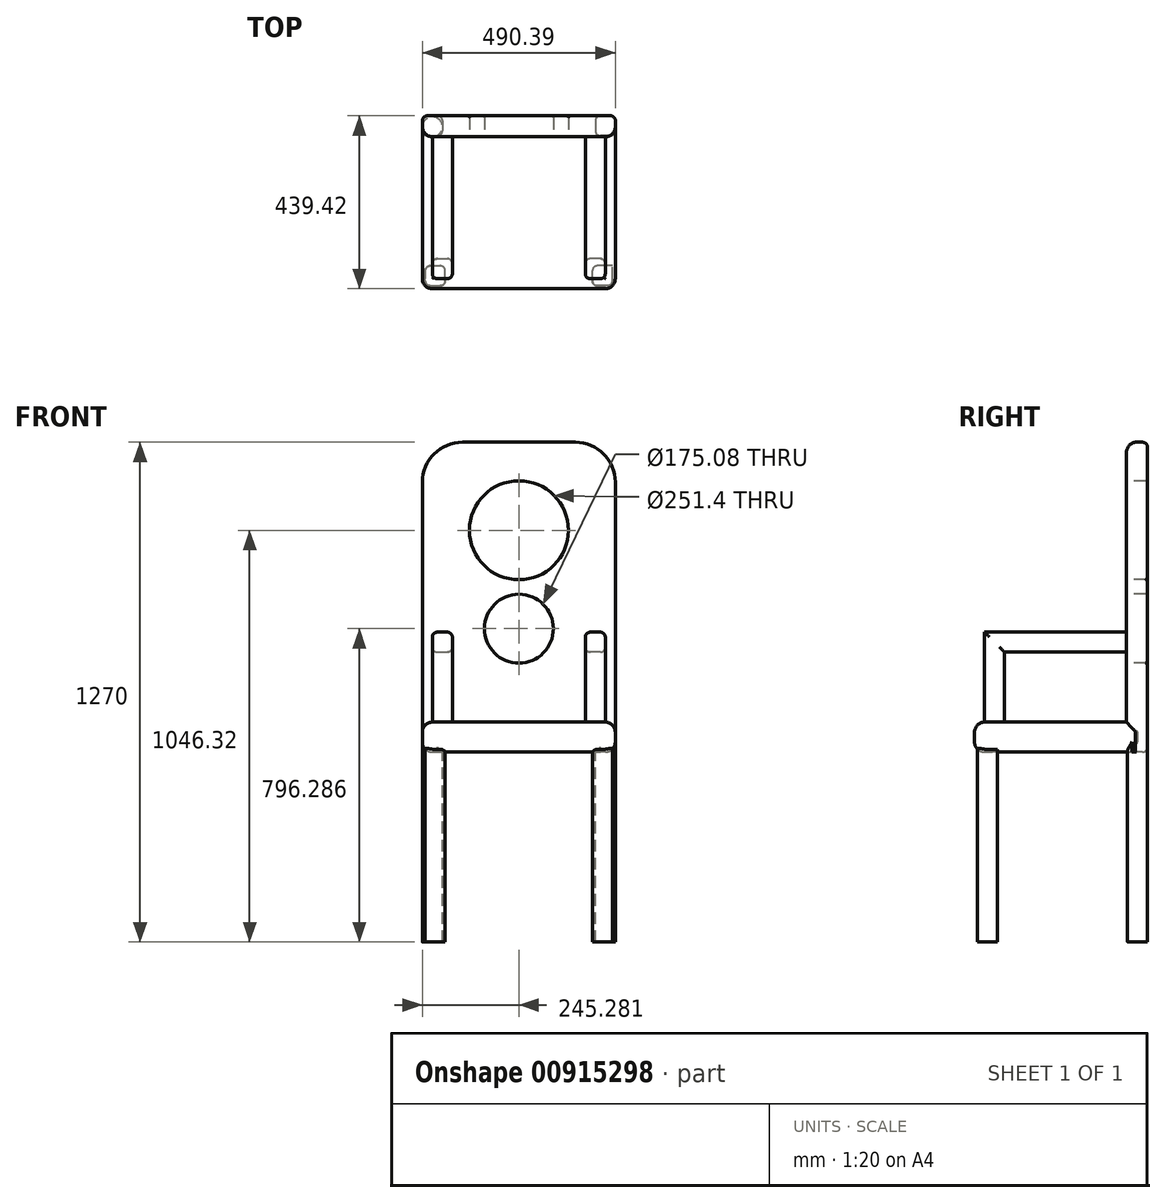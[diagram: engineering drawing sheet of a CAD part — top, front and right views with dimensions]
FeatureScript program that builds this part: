
annotation { "Feature Type Name" : "Feature", "Feature Type Description" : "" }
export const myFeature = defineFeature(function(context is Context, id is Id, definition is map)
    precondition{}
    {
        {
            var Q0;
            Q0=qCreatedBy(makeId("Top.planeOp"),FACE);
            var sketch = newSketch(context, id + "F0", { "sketchPlane" : qUnion([Q0])});
            skLineSegment(sketch, "E0.bottom", {"start": v(-206.15, 232.77) * mm, "end": v(284.07, 232.77) * mm});
            skLineSegment(sketch, "E0.top", {"start": v(-206.15, -181.25) * mm, "end": v(284.07, -181.25) * mm});
            skLineSegment(sketch, "E0.left", {"start": v(-206.15, 232.77) * mm, "end": v(-206.15, -181.25) * mm});
            skLineSegment(sketch, "E0.right", {"start": v(284.07, 232.77) * mm, "end": v(284.07, -181.25) * mm});
            skSolve(sketch);
        }
        {
            var Q0;
            Q0 = qSketchRegion(id + "F0", true);
            extrude(context, id + "F1", {"entities" : qUnion([Q0]), "depth" : 76.2 * mm, "offsetDistance" : 25.4 * mm});
        }
        {
            var Q0;
            Q0=makeQuery(id+"F1.opExtrude","CAP_EDGE",EDGE,{"disambiguationData":[OSD([sQuery(id+"F0.wireOp",EDGE,"E0.top")])],"isStart":false});
            var Q1;
            Q1=makeQuery(id+"F1.opExtrude","CAP_EDGE",EDGE,{"disambiguationData":[OSD([sQuery(id+"F0.wireOp",EDGE,"E0.left")])],"isStart":false});
            var Q2;
            Q2=makeQuery(id+"F1.opExtrude","SWEPT_EDGE",EDGE,{"disambiguationData":[OSD([sQuery(id+"F0.wireOp",EDGE,"E0.top"),sQuery(id+"F0.wireOp",EDGE,"E0.left")])]});
            var Q3;
            Q3=makeQuery(id+"F1.opExtrude","SWEPT_EDGE",EDGE,{"disambiguationData":[OSD([sQuery(id+"F0.wireOp",EDGE,"E0.top"),sQuery(id+"F0.wireOp",EDGE,"E0.right")])]});
            var Q4;
            Q4=makeQuery(id+"F1.opExtrude","CAP_EDGE",EDGE,{"disambiguationData":[OSD([sQuery(id+"F0.wireOp",EDGE,"E0.right")])],"isStart":false});
            fillet(context, id + "F2", {"entities" : qUnion([Q0, Q1, Q2, Q3, Q4]), "radius" : 25.4 * mm, "tangentPropagation" : true, "allowEdgeOverflow" : false});
        }
        {
            var Q0;
            Q0=makeQuery(id+"F1.opExtrude","SWEPT_FACE",FACE,{"disambiguationData":[OSD([sQuery(id+"F0.wireOp",EDGE,"E0.bottom")])]});
            cPlane(context, id + "F3", {"entities" : qUnion([Q0]), "cplaneType" : CPlaneType.OFFSET, "offset" : 25.4 * mm, "width" : 152.4 * mm, "height" : 152.4 * mm});
        }
        {
            var Q0;
            Q0=qCreatedBy(id+"F3.planeOp",FACE);
            var sketch = newSketch(context, id + "F4", { "sketchPlane" : qUnion([Q0])});
            skLineSegment(sketch, "E1.bottom", {"start": v(-284.24, 0) * mm, "end": v(205.98, 0) * mm});
            skLineSegment(sketch, "E1.top", {"start": v(-284.24, 787.4) * mm, "end": v(205.98, 787.4) * mm});
            skLineSegment(sketch, "E1.left", {"start": v(-284.24, 0) * mm, "end": v(-284.24, 787.4) * mm});
            skLineSegment(sketch, "E1.right", {"start": v(205.98, 0) * mm, "end": v(205.98, 787.4) * mm});
            skSolve(sketch);
        }
        {
            var Q0;
            Q0 = qSketchRegion(id + "F4", true);
            extrude(context, id + "F5", {"entities" : qUnion([Q0]), "operationType" : NewBodyOperationType.ADD, "oppositeDirection" : true, "depth" : 53.34 * mm, "offsetDistance" : 25.4 * mm});
        }
        {
            var Q0;
            Q0=makeQuery(id+"F5.opExtrude","SWEPT_EDGE",EDGE,{"disambiguationData":[OSD([sQuery(id+"F4.wireOp",EDGE,"E1.top"),sQuery(id+"F4.wireOp",EDGE,"E1.left")])]});
            var Q1;
            Q1=makeQuery(id+"F5.opExtrude","SWEPT_EDGE",EDGE,{"disambiguationData":[OSD([sQuery(id+"F4.wireOp",EDGE,"E1.top"),sQuery(id+"F4.wireOp",EDGE,"E1.right")])]});
            fillet(context, id + "F6", {"entities" : qUnion([Q0, Q1]), "radius" : 101.6 * mm, "tangentPropagation" : true, "allowEdgeOverflow" : false});
        }
        {
            var Q0;
            Q0=makeQuery(id+"F5.opExtrude","CAP_EDGE",EDGE,{"disambiguationData":[OSD([sQuery(id+"F4.wireOp",EDGE,"E1.left")])],"isStart":false});
            fillet(context, id + "F7", {"entities" : qUnion([Q0]), "radius" : 25.4 * mm, "tangentPropagation" : true, "allowEdgeOverflow" : false});
        }
        {
            var Q0;
            Q0=makeQuery(id+"F5.boolean.opBoolean","MERGE",FACE,{"derivedFrom":[makeQuery(id+"F1.opExtrude","CAP_FACE",FACE,{"disambiguationData":[OSD([sQuery(id+"F0.wireOp",EDGE,"E0.bottom"),sQuery(id+"F0.wireOp",EDGE,"E0.top"),sQuery(id+"F0.wireOp",EDGE,"E0.left"),sQuery(id+"F0.wireOp",EDGE,"E0.right")])],"isStart":true}),makeQuery(id+"F5.opExtrude","SWEPT_FACE",FACE,{"disambiguationData":[OSD([sQuery(id+"F4.wireOp",EDGE,"E1.bottom")])]})]});
            var sketch = newSketch(context, id + "F8", { "sketchPlane" : qUnion([Q0])});
            skLineSegment(sketch, "E2.bottom", {"start": v(-198.7, 173.81) * mm, "end": v(-147.9, 173.81) * mm});
            skLineSegment(sketch, "E2.top", {"start": v(-198.7, 123.01) * mm, "end": v(-147.9, 123.01) * mm});
            skLineSegment(sketch, "E2.left", {"start": v(-198.7, 173.81) * mm, "end": v(-198.7, 123.01) * mm});
            skLineSegment(sketch, "E2.right", {"start": v(-147.9, 173.81) * mm, "end": v(-147.9, 123.01) * mm});
            skLineSegment(sketch, "E3.bottom", {"start": v(276.63, 173.81) * mm, "end": v(225.83, 173.81) * mm});
            skLineSegment(sketch, "E3.top", {"start": v(276.63, 123.01) * mm, "end": v(225.83, 123.01) * mm});
            skLineSegment(sketch, "E3.left", {"start": v(276.63, 173.81) * mm, "end": v(276.63, 123.01) * mm});
            skLineSegment(sketch, "E3.right", {"start": v(225.83, 173.81) * mm, "end": v(225.83, 123.01) * mm});
            skLineSegment(sketch, "E4.bottom", {"start": v(284.24, -258.17) * mm, "end": v(233.44, -258.17) * mm});
            skLineSegment(sketch, "E4.top", {"start": v(284.24, -207.37) * mm, "end": v(233.44, -207.37) * mm});
            skLineSegment(sketch, "E4.left", {"start": v(284.24, -258.17) * mm, "end": v(284.24, -207.37) * mm});
            skLineSegment(sketch, "E4.right", {"start": v(233.44, -258.17) * mm, "end": v(233.44, -207.37) * mm});
            skLineSegment(sketch, "E5.bottom", {"start": v(-205.98, -258.17) * mm, "end": v(-155.18, -258.17) * mm});
            skLineSegment(sketch, "E5.top", {"start": v(-205.98, -207.37) * mm, "end": v(-155.18, -207.37) * mm});
            skLineSegment(sketch, "E5.left", {"start": v(-205.98, -258.17) * mm, "end": v(-205.98, -207.37) * mm});
            skLineSegment(sketch, "E5.right", {"start": v(-155.18, -258.17) * mm, "end": v(-155.18, -207.37) * mm});
            skSolve(sketch);
        }
        {
            var Q0;
            Q0 = qSketchRegion(id + "F8", true);
            extrude(context, id + "F9", {"entities" : qUnion([Q0]), "operationType" : NewBodyOperationType.ADD, "depth" : 482.6 * mm, "offsetDistance" : 25.4 * mm});
        }
        {
            var Q0;
            Q0=makeQuery(id+"F5.opExtrude","CAP_FACE",FACE,{"disambiguationData":[OSD([sQuery(id+"F4.wireOp",EDGE,"E1.bottom"),sQuery(id+"F4.wireOp",EDGE,"E1.top"),sQuery(id+"F4.wireOp",EDGE,"E1.left"),sQuery(id+"F4.wireOp",EDGE,"E1.right")])],"isStart":false});
            var sketch = newSketch(context, id + "F10", { "sketchPlane" : qUnion([Q0])});
            skCircle(sketch, "E6", {"center": v(39.13, 563.72) * mm, "radius": 125.7 * mm});
            skPoint(sketch, "E6.centerSnap0", {"position": v(39.13, 762) * mm});
            skCircle(sketch, "E7", {"center": v(39.13, 313.69) * mm, "radius": 87.54 * mm});
            skSolve(sketch);
        }
        {
            var Q0;
            Q0 = qSketchRegion(id + "F10", true);
            extrude(context, id + "F11", {"entities" : qUnion([Q0]), "operationType" : NewBodyOperationType.REMOVE, "oppositeDirection" : true, "depth" : 320.04 * mm, "offsetDistance" : 25.4 * mm});
        }
        {
            var Q0;
            Q0=makeQuery(id+"F9.opExtrude","SWEPT_EDGE",EDGE,{"disambiguationData":[OSD([sQuery(id+"F0.wireOp",EDGE,"E0.bottom"),sQuery(id+"F0.wireOp",EDGE,"E0.top"),sQuery(id+"F0.wireOp",EDGE,"E0.left"),sQuery(id+"F0.wireOp",EDGE,"E0.right"),sQuery(id+"F8.wireOp",EDGE,"E2.bottom"),sQuery(id+"F8.wireOp",EDGE,"E2.left")])]});
            var Q1;
            Q1=makeQuery(id+"F9.opExtrude","SWEPT_EDGE",EDGE,{"disambiguationData":[OSD([sQuery(id+"F8.wireOp",EDGE,"E2.bottom"),sQuery(id+"F8.wireOp",EDGE,"E2.right")])]});
            var Q2;
            Q2=makeQuery(id+"F9.opExtrude","SWEPT_EDGE",EDGE,{"disambiguationData":[OSD([sQuery(id+"F8.wireOp",EDGE,"E2.top"),sQuery(id+"F8.wireOp",EDGE,"E2.right")])]});
            var Q3;
            Q3=makeQuery(id+"F9.opExtrude","SWEPT_EDGE",EDGE,{"disambiguationData":[OSD([sQuery(id+"F8.wireOp",EDGE,"E2.top"),sQuery(id+"F8.wireOp",EDGE,"E2.left")])]});
            var Q4;
            Q4=makeQuery(id+"F9.opExtrude","SWEPT_EDGE",EDGE,{"disambiguationData":[OSD([sQuery(id+"F8.wireOp",EDGE,"E5.top"),sQuery(id+"F8.wireOp",EDGE,"E5.left")])]});
            var Q5;
            Q5=makeQuery(id+"F9.opExtrude","SWEPT_EDGE",EDGE,{"disambiguationData":[OSD([sQuery(id+"F8.wireOp",EDGE,"E5.top"),sQuery(id+"F8.wireOp",EDGE,"E5.right")])]});
            var Q6;
            Q6=makeQuery(id+"F9.boolean.opBoolean","MERGE",EDGE,{"derivedFrom":[makeQuery(id+"F5.opExtrude","CAP_EDGE",EDGE,{"disambiguationData":[OSD([sQuery(id+"F4.wireOp",EDGE,"E1.right")])],"isStart":true}),makeQuery(id+"F9.opExtrude","SWEPT_EDGE",EDGE,{"disambiguationData":[OSD([sQuery(id+"F8.wireOp",EDGE,"E5.bottom"),sQuery(id+"F8.wireOp",EDGE,"E5.left")])]})]});
            var Q7;
            Q7=makeQuery(id+"F9.opExtrude","SWEPT_EDGE",EDGE,{"disambiguationData":[OSD([sQuery(id+"F4.wireOp",EDGE,"E1.bottom"),sQuery(id+"F8.wireOp",EDGE,"E5.bottom"),sQuery(id+"F8.wireOp",EDGE,"E5.right")])]});
            var Q8;
            Q8=makeQuery(id+"F5.opExtrude","CAP_EDGE",EDGE,{"disambiguationData":[OSD([sQuery(id+"F4.wireOp",EDGE,"E1.bottom")])],"isStart":true});
            var Q9;
            Q9=makeQuery(id+"F9.opExtrude","SWEPT_EDGE",EDGE,{"disambiguationData":[OSD([sQuery(id+"F4.wireOp",EDGE,"E1.bottom"),sQuery(id+"F8.wireOp",EDGE,"E4.bottom"),sQuery(id+"F8.wireOp",EDGE,"E4.right")])]});
            var Q10;
            Q10=makeQuery(id+"F9.boolean.opBoolean","MERGE",EDGE,{"derivedFrom":[makeQuery(id+"F5.opExtrude","CAP_EDGE",EDGE,{"disambiguationData":[OSD([sQuery(id+"F4.wireOp",EDGE,"E1.left")])],"isStart":true}),makeQuery(id+"F9.opExtrude","SWEPT_EDGE",EDGE,{"disambiguationData":[OSD([sQuery(id+"F8.wireOp",EDGE,"E4.bottom"),sQuery(id+"F8.wireOp",EDGE,"E4.left")])]})]});
            var Q11;
            Q11=makeQuery(id+"F9.opExtrude","SWEPT_EDGE",EDGE,{"disambiguationData":[OSD([sQuery(id+"F8.wireOp",EDGE,"E4.top"),sQuery(id+"F8.wireOp",EDGE,"E4.left")])]});
            var Q12;
            Q12=makeQuery(id+"F9.opExtrude","SWEPT_EDGE",EDGE,{"disambiguationData":[OSD([sQuery(id+"F8.wireOp",EDGE,"E4.top"),sQuery(id+"F8.wireOp",EDGE,"E4.right")])]});
            var Q13;
            Q13=makeQuery(id+"F9.opExtrude","SWEPT_EDGE",EDGE,{"disambiguationData":[OSD([sQuery(id+"F8.wireOp",EDGE,"E3.bottom"),sQuery(id+"F8.wireOp",EDGE,"E3.right")])]});
            var Q14;
            Q14=makeQuery(id+"F9.opExtrude","SWEPT_EDGE",EDGE,{"disambiguationData":[OSD([sQuery(id+"F8.wireOp",EDGE,"E3.top"),sQuery(id+"F8.wireOp",EDGE,"E3.right")])]});
            var Q15;
            Q15=makeQuery(id+"F9.opExtrude","SWEPT_EDGE",EDGE,{"disambiguationData":[OSD([sQuery(id+"F0.wireOp",EDGE,"E0.bottom"),sQuery(id+"F0.wireOp",EDGE,"E0.top"),sQuery(id+"F0.wireOp",EDGE,"E0.left"),sQuery(id+"F0.wireOp",EDGE,"E0.right"),sQuery(id+"F8.wireOp",EDGE,"E3.bottom"),sQuery(id+"F8.wireOp",EDGE,"E3.left")])]});
            fillet(context, id + "F12", {"entities" : qUnion([Q0, Q1, Q2, Q3, Q4, Q5, Q6, Q7, Q8, Q9, Q10, Q11, Q12, Q13, Q14, Q15]), "radius" : 12.7 * mm, "tangentPropagation" : true, "allowEdgeOverflow" : false});
        }
        {
            var Q0;
            Q0=makeQuery(id+"F1.opExtrude","CAP_EDGE",EDGE,{"disambiguationData":[OSD([sQuery(id+"F0.wireOp",EDGE,"E0.top")])],"isStart":true});
            fillet(context, id + "F13", {"entities" : qUnion([Q0]), "radius" : 25.4 * mm, "tangentPropagation" : true, "allowEdgeOverflow" : false});
        }
        {
            var Q0;
            Q0=makeQuery(id+"F11.boolean.opBoolean","COPY",EDGE,{"derivedFrom":makeQuery(id+"F11.opExtrude","CAP_EDGE",EDGE,{"disambiguationData":[OSD([sQuery(id+"F10.wireOp",EDGE,"E6")])],"isStart":true})});
            var Q1;
            Q1=makeQuery(id+"F11.boolean.opBoolean","INTERSECT",EDGE,{"derivedFrom":[makeQuery(id+"F9.boolean.opBoolean","MERGE",FACE,{"derivedFrom":[makeQuery(id+"F5.opExtrude","CAP_FACE",FACE,{"disambiguationData":[OSD([sQuery(id+"F4.wireOp",EDGE,"E1.bottom"),sQuery(id+"F4.wireOp",EDGE,"E1.top"),sQuery(id+"F4.wireOp",EDGE,"E1.left"),sQuery(id+"F4.wireOp",EDGE,"E1.right")])],"isStart":true}),makeQuery(id+"F9.opExtrude","SWEPT_FACE",FACE,{"disambiguationData":[OSD([sQuery(id+"F8.wireOp",EDGE,"E4.bottom")])]}),makeQuery(id+"F9.opExtrude","SWEPT_FACE",FACE,{"disambiguationData":[OSD([sQuery(id+"F8.wireOp",EDGE,"E5.bottom")])]})]}),makeQuery(id+"F11.opExtrude","SWEPT_FACE",FACE,{"disambiguationData":[OSD([sQuery(id+"F10.wireOp",EDGE,"E6")])]})]});
            fillet(context, id + "F14", {"entities" : qUnion([Q0, Q1]), "radius" : 5.08 * mm, "tangentPropagation" : true, "allowEdgeOverflow" : false});
        }
        {
            var Q0;
            Q0=makeQuery(id+"F1.opExtrude","CAP_FACE",FACE,{"disambiguationData":[OSD([sQuery(id+"F0.wireOp",EDGE,"E0.bottom"),sQuery(id+"F0.wireOp",EDGE,"E0.top"),sQuery(id+"F0.wireOp",EDGE,"E0.left"),sQuery(id+"F0.wireOp",EDGE,"E0.right")])],"isStart":false});
            var sketch = newSketch(context, id + "F15", { "sketchPlane" : qUnion([Q0])});
            skLineSegment(sketch, "E8.bottom", {"start": v(258.67, -155.85) * mm, "end": v(207.87, -155.85) * mm});
            skLineSegment(sketch, "E8.top", {"start": v(258.67, -105.05) * mm, "end": v(207.87, -105.05) * mm});
            skLineSegment(sketch, "E8.left", {"start": v(258.67, -155.85) * mm, "end": v(258.67, -105.05) * mm});
            skLineSegment(sketch, "E8.right", {"start": v(207.87, -155.85) * mm, "end": v(207.87, -105.05) * mm});
            skLineSegment(sketch, "E9.bottom", {"start": v(-180.75, -155.85) * mm, "end": v(-129.95, -155.85) * mm});
            skLineSegment(sketch, "E9.top", {"start": v(-180.75, -105.05) * mm, "end": v(-129.95, -105.05) * mm});
            skLineSegment(sketch, "E9.left", {"start": v(-180.75, -155.85) * mm, "end": v(-180.75, -105.05) * mm});
            skLineSegment(sketch, "E9.right", {"start": v(-129.95, -155.85) * mm, "end": v(-129.95, -105.05) * mm});
            skSolve(sketch);
        }
        {
            var Q0;
            Q0 = qSketchRegion(id + "F15", true);
            extrude(context, id + "F16", {"entities" : qUnion([Q0]), "operationType" : NewBodyOperationType.ADD, "depth" : 228.6 * mm, "offsetDistance" : 25.4 * mm});
        }
        {
            var Q0;
            Q0=makeQuery(id+"F16.opExtrude","SWEPT_FACE",FACE,{"disambiguationData":[OSD([sQuery(id+"F15.wireOp",EDGE,"E9.top")])]});
            var sketch = newSketch(context, id + "F17", { "sketchPlane" : qUnion([Q0])});
            skLineSegment(sketch, "E10.bottom", {"start": v(129.95, 304.8) * mm, "end": v(180.75, 304.8) * mm});
            skLineSegment(sketch, "E10.top", {"start": v(129.95, 254) * mm, "end": v(180.75, 254) * mm});
            skLineSegment(sketch, "E10.left", {"start": v(129.95, 304.8) * mm, "end": v(129.95, 254) * mm});
            skLineSegment(sketch, "E10.right", {"start": v(180.75, 304.8) * mm, "end": v(180.75, 254) * mm});
            skSolve(sketch);
        }
        {
            var Q0;
            Q0 = qSketchRegion(id + "F17", true);
            extrude(context, id + "F18", {"entities" : qUnion([Q0]), "operationType" : NewBodyOperationType.ADD, "depth" : 355.6 * mm, "offsetDistance" : 25.4 * mm});
        }
        {
            var Q0;
            Q0=makeQuery(id+"F16.opExtrude","SWEPT_FACE",FACE,{"disambiguationData":[OSD([sQuery(id+"F15.wireOp",EDGE,"E8.top")])]});
            var sketch = newSketch(context, id + "F19", { "sketchPlane" : qUnion([Q0])});
            skLineSegment(sketch, "E11.bottom", {"start": v(-258.67, 304.8) * mm, "end": v(-207.87, 304.8) * mm});
            skLineSegment(sketch, "E11.top", {"start": v(-258.67, 254) * mm, "end": v(-207.87, 254) * mm});
            skLineSegment(sketch, "E11.left", {"start": v(-258.67, 304.8) * mm, "end": v(-258.67, 254) * mm});
            skLineSegment(sketch, "E11.right", {"start": v(-207.87, 304.8) * mm, "end": v(-207.87, 254) * mm});
            skSolve(sketch);
        }
        {
            var Q0;
            Q0 = qSketchRegion(id + "F19", true);
            extrude(context, id + "F20", {"entities" : qUnion([Q0]), "operationType" : NewBodyOperationType.ADD, "depth" : 355.6 * mm, "offsetDistance" : 25.4 * mm});
        }
        {
            var Q0;
            Q0=makeQuery(id+"F16.opExtrude","SWEPT_EDGE",EDGE,{"disambiguationData":[OSD([sQuery(id+"F0.wireOp",EDGE,"E0.bottom"),sQuery(id+"F0.wireOp",EDGE,"E0.top"),sQuery(id+"F0.wireOp",EDGE,"E0.left"),sQuery(id+"F0.wireOp",EDGE,"E0.right"),sQuery(id+"F15.wireOp",EDGE,"E9.bottom"),sQuery(id+"F15.wireOp",EDGE,"E9.right")])]});
            var Q1;
            Q1=makeQuery(id+"F16.opExtrude","SWEPT_EDGE",EDGE,{"disambiguationData":[OSD([sQuery(id+"F15.wireOp",EDGE,"E9.bottom"),sQuery(id+"F15.wireOp",EDGE,"E9.left")])]});
            var Q2;
            Q2=makeQuery(id+"F16.opExtrude","SWEPT_EDGE",EDGE,{"disambiguationData":[OSD([sQuery(id+"F0.wireOp",EDGE,"E0.bottom"),sQuery(id+"F0.wireOp",EDGE,"E0.top"),sQuery(id+"F0.wireOp",EDGE,"E0.left"),sQuery(id+"F0.wireOp",EDGE,"E0.right"),sQuery(id+"F15.wireOp",EDGE,"E9.top"),sQuery(id+"F15.wireOp",EDGE,"E9.left")])]});
            var Q3;
            Q3=makeQuery(id+"F18.opExtrude","SWEPT_EDGE",EDGE,{"disambiguationData":[OSD([sQuery(id+"F0.wireOp",EDGE,"E0.bottom"),sQuery(id+"F0.wireOp",EDGE,"E0.top"),sQuery(id+"F0.wireOp",EDGE,"E0.left"),sQuery(id+"F0.wireOp",EDGE,"E0.right"),sQuery(id+"F15.wireOp",EDGE,"E9.top"),sQuery(id+"F15.wireOp",EDGE,"E9.left"),sQuery(id+"F17.wireOp",EDGE,"E10.top"),sQuery(id+"F17.wireOp",EDGE,"E10.right")])]});
            var Q4;
            Q4=makeQuery(id+"F18.boolean.opBoolean","MERGE",EDGE,{"derivedFrom":[makeQuery(id+"F16.opExtrude","CAP_EDGE",EDGE,{"disambiguationData":[OSD([sQuery(id+"F15.wireOp",EDGE,"E9.left")])],"isStart":false}),makeQuery(id+"F18.opExtrude","SWEPT_EDGE",EDGE,{"disambiguationData":[OSD([sQuery(id+"F17.wireOp",EDGE,"E10.bottom"),sQuery(id+"F17.wireOp",EDGE,"E10.right")])]})]});
            var Q5;
            Q5=makeQuery(id+"F18.boolean.opBoolean","MERGE",EDGE,{"derivedFrom":[makeQuery(id+"F16.opExtrude","CAP_EDGE",EDGE,{"disambiguationData":[OSD([sQuery(id+"F15.wireOp",EDGE,"E9.right")])],"isStart":false}),makeQuery(id+"F18.opExtrude","SWEPT_EDGE",EDGE,{"disambiguationData":[OSD([sQuery(id+"F17.wireOp",EDGE,"E10.bottom"),sQuery(id+"F17.wireOp",EDGE,"E10.left")])]})]});
            var Q6;
            Q6=makeQuery(id+"F18.opExtrude","SWEPT_EDGE",EDGE,{"disambiguationData":[OSD([sQuery(id+"F15.wireOp",EDGE,"E9.top"),sQuery(id+"F15.wireOp",EDGE,"E9.right"),sQuery(id+"F17.wireOp",EDGE,"E10.top"),sQuery(id+"F17.wireOp",EDGE,"E10.left")])]});
            var Q7;
            Q7=makeQuery(id+"F16.opExtrude","SWEPT_EDGE",EDGE,{"disambiguationData":[OSD([sQuery(id+"F15.wireOp",EDGE,"E9.top"),sQuery(id+"F15.wireOp",EDGE,"E9.right")])]});
            var Q8;
            Q8=makeQuery(id+"F20.boolean.opBoolean","MERGE",EDGE,{"derivedFrom":[makeQuery(id+"F16.opExtrude","CAP_EDGE",EDGE,{"disambiguationData":[OSD([sQuery(id+"F15.wireOp",EDGE,"E8.left")])],"isStart":false}),makeQuery(id+"F20.opExtrude","SWEPT_EDGE",EDGE,{"disambiguationData":[OSD([sQuery(id+"F19.wireOp",EDGE,"E11.bottom"),sQuery(id+"F19.wireOp",EDGE,"E11.left")])]})]});
            var Q9;
            Q9=makeQuery(id+"F20.boolean.opBoolean","MERGE",EDGE,{"derivedFrom":[makeQuery(id+"F16.opExtrude","CAP_EDGE",EDGE,{"disambiguationData":[OSD([sQuery(id+"F15.wireOp",EDGE,"E8.right")])],"isStart":false}),makeQuery(id+"F20.opExtrude","SWEPT_EDGE",EDGE,{"disambiguationData":[OSD([sQuery(id+"F19.wireOp",EDGE,"E11.bottom"),sQuery(id+"F19.wireOp",EDGE,"E11.right")])]})]});
            var Q10;
            Q10=makeQuery(id+"F16.opExtrude","SWEPT_EDGE",EDGE,{"disambiguationData":[OSD([sQuery(id+"F0.wireOp",EDGE,"E0.bottom"),sQuery(id+"F0.wireOp",EDGE,"E0.top"),sQuery(id+"F0.wireOp",EDGE,"E0.left"),sQuery(id+"F0.wireOp",EDGE,"E0.right"),sQuery(id+"F15.wireOp",EDGE,"E8.bottom"),sQuery(id+"F15.wireOp",EDGE,"E8.right")])]});
            var Q11;
            Q11=makeQuery(id+"F16.opExtrude","SWEPT_EDGE",EDGE,{"disambiguationData":[OSD([sQuery(id+"F15.wireOp",EDGE,"E8.bottom"),sQuery(id+"F15.wireOp",EDGE,"E8.left")])]});
            var Q12;
            Q12=makeQuery(id+"F16.opExtrude","SWEPT_EDGE",EDGE,{"disambiguationData":[OSD([sQuery(id+"F0.wireOp",EDGE,"E0.bottom"),sQuery(id+"F0.wireOp",EDGE,"E0.top"),sQuery(id+"F0.wireOp",EDGE,"E0.left"),sQuery(id+"F0.wireOp",EDGE,"E0.right"),sQuery(id+"F15.wireOp",EDGE,"E8.top"),sQuery(id+"F15.wireOp",EDGE,"E8.left")])]});
            var Q13;
            Q13=makeQuery(id+"F20.opExtrude","SWEPT_EDGE",EDGE,{"disambiguationData":[OSD([sQuery(id+"F0.wireOp",EDGE,"E0.bottom"),sQuery(id+"F0.wireOp",EDGE,"E0.top"),sQuery(id+"F0.wireOp",EDGE,"E0.left"),sQuery(id+"F0.wireOp",EDGE,"E0.right"),sQuery(id+"F15.wireOp",EDGE,"E8.top"),sQuery(id+"F15.wireOp",EDGE,"E8.left"),sQuery(id+"F19.wireOp",EDGE,"E11.top"),sQuery(id+"F19.wireOp",EDGE,"E11.left")])]});
            var Q14;
            Q14=makeQuery(id+"F20.opExtrude","SWEPT_EDGE",EDGE,{"disambiguationData":[OSD([sQuery(id+"F15.wireOp",EDGE,"E8.top"),sQuery(id+"F15.wireOp",EDGE,"E8.right"),sQuery(id+"F19.wireOp",EDGE,"E11.top"),sQuery(id+"F19.wireOp",EDGE,"E11.right")])]});
            var Q15;
            Q15=makeQuery(id+"F16.opExtrude","SWEPT_EDGE",EDGE,{"disambiguationData":[OSD([sQuery(id+"F15.wireOp",EDGE,"E8.top"),sQuery(id+"F15.wireOp",EDGE,"E8.right")])]});
            fillet(context, id + "F21", {"entities" : qUnion([Q0, Q1, Q2, Q3, Q4, Q5, Q6, Q7, Q8, Q9, Q10, Q11, Q12, Q13, Q14, Q15]), "radius" : 12.7 * mm, "tangentPropagation" : true, "allowEdgeOverflow" : false});
        }
        {
            var Q0;
            Q0=makeQuery(id+"F11.boolean.opBoolean","INTERSECT",EDGE,{"derivedFrom":[makeQuery(id+"F9.boolean.opBoolean","MERGE",FACE,{"derivedFrom":[makeQuery(id+"F5.opExtrude","CAP_FACE",FACE,{"disambiguationData":[OSD([sQuery(id+"F4.wireOp",EDGE,"E1.bottom"),sQuery(id+"F4.wireOp",EDGE,"E1.top"),sQuery(id+"F4.wireOp",EDGE,"E1.left"),sQuery(id+"F4.wireOp",EDGE,"E1.right")])],"isStart":true}),makeQuery(id+"F9.opExtrude","SWEPT_FACE",FACE,{"disambiguationData":[OSD([sQuery(id+"F8.wireOp",EDGE,"E4.bottom")])]}),makeQuery(id+"F9.opExtrude","SWEPT_FACE",FACE,{"disambiguationData":[OSD([sQuery(id+"F8.wireOp",EDGE,"E5.bottom")])]})]}),makeQuery(id+"F11.opExtrude","SWEPT_FACE",FACE,{"disambiguationData":[OSD([sQuery(id+"F10.wireOp",EDGE,"E7")])]})]});
            var Q1;
            Q1=makeQuery(id+"F11.boolean.opBoolean","COPY",EDGE,{"derivedFrom":makeQuery(id+"F11.opExtrude","CAP_EDGE",EDGE,{"disambiguationData":[OSD([sQuery(id+"F10.wireOp",EDGE,"E7")])],"isStart":true})});
            fillet(context, id + "F22", {"entities" : qUnion([Q0, Q1]), "radius" : 5.08 * mm, "tangentPropagation" : true, "allowEdgeOverflow" : false});
        }
    });
